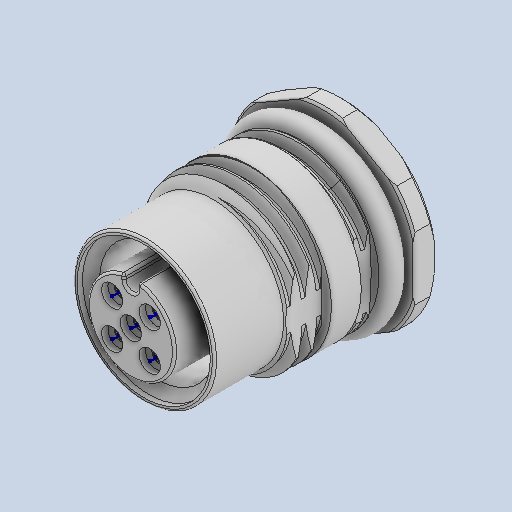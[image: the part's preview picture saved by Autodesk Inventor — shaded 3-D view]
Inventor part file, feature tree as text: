
AUTODESK INVENTOR PART (.ipt)
format: ipt  version: 2024.2 (Build 282272000, 272)  size: 804,352 bytes
history: native  units: mm
features: sketch x2, other x1, extrude x1, projected_geometry x1, imported_body x1
ambient origin geometry x8: Origin, YZ Plane, XZ Plane, XY Plane, X Axis, Y Axis, Z Axis, Center Point
bodies: Solid1 (feature_tree)
feature tree (6):
  other  "Repaired Geometry1"
  extrude  "Extrusion1"  [1 undecoded]
  sketch  "3D Sketch1"
  sketch  "Sketch2"  dims[d0=10.0mm d1=0.0mm]
  projected_geometry  "Projected Loop1"
  imported_body  "Base1"
note: 1 required parameter value undecoded (feature->parameter linkage not recoverable at this tier; creation-order binding heuristic only, values carry confidence <= 0.55)
